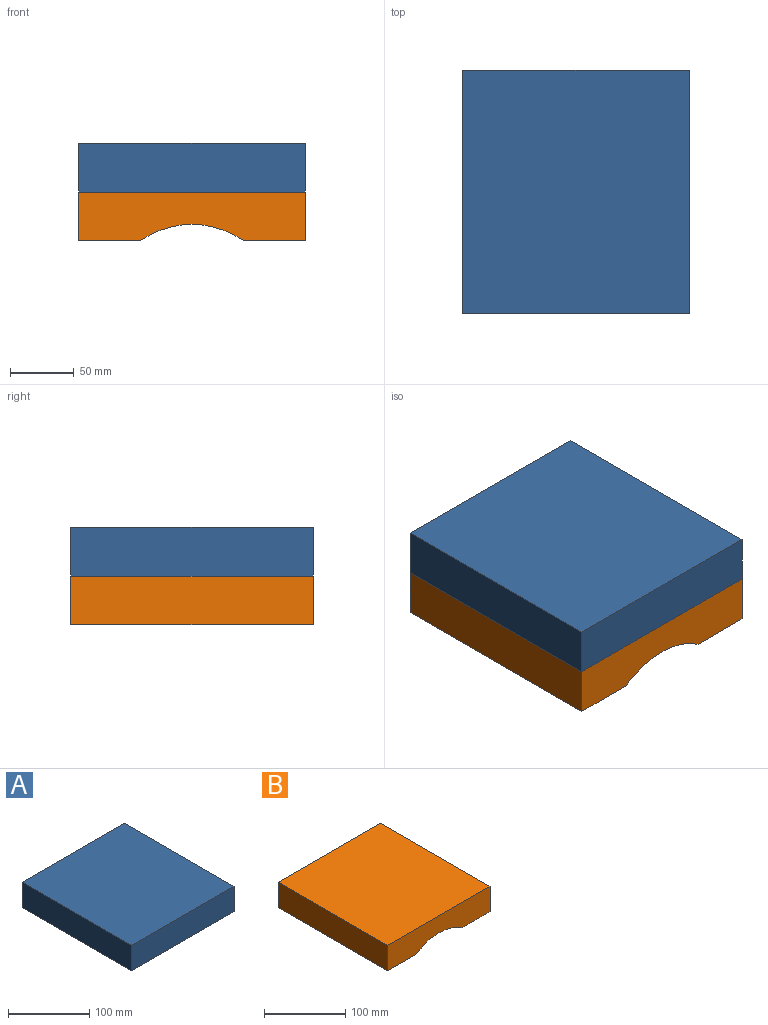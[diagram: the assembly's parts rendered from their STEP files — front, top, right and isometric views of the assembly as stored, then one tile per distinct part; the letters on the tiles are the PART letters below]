
ASSEMBLY  parts=2 mates=1
PART A: 6 faces, bbox 177.8x190.5x38.1 mm
  f0: plane 190.5x177.8mm, normal (0,0,-1), area 33870.9mm2, adj f1,f3,f4,f5
  f1: plane 190.5x38.1mm, normal (1,0,0), area 7258mm2, adj f0,f2,f4,f5
  f2: plane 190.5x177.8mm, normal (0,0,1), area 33870.9mm2, adj f1,f3,f4,f5
  f3: plane 190.5x38.1mm, normal (-1,0,0), area 7258mm2, adj f0,f2,f4,f5
  f4: plane 177.8x38.1mm, normal (0,1,0), area 6774.2mm2, adj f0,f1,f2,f3
  f5: plane 177.8x38.1mm, normal (0,-1,0), area 6774.2mm2, adj f0,f1,f2,f3
PART B: 8 faces, bbox 177.8x190.5x38.1 mm
  f0: plane 190.5x38.1mm, normal (-1,0,0), area 7258mm2, adj f1,f5,f6,f7
  f1: plane 190.5x48.74mm, normal (0,0,-1), area 9284.8mm2, adj f0,f2,f6,f7
  f2: cylinder r=69.85mm len=190.5mm, axis (0,-1,0), area 16301.8mm2, adj f1,f3,f6,f7
  f3: plane 190.5x48.74mm, normal (0,0,-1), area 9284.8mm2, adj f2,f4,f6,f7
  f4: plane 190.5x38.1mm, normal (1,0,0), area 7258mm2, adj f3,f5,f6,f7
  f5: plane 190.5x177.8mm, normal (0,0,1), area 33870.9mm2, adj f0,f4,f6,f7
  f6: plane 177.8x38.1mm, normal (0,1,0), area 6080.7mm2, adj f0,f1,f2,f3,f4,f5
  f7: plane 177.8x38.1mm, normal (0,-1,0), area 6080.7mm2, adj f0,f1,f2,f3,f4,f5
PLACE A t=(31.26,-75.65,12.87)mm
PLACE B t=(-57.64,-75.65,-44.28)mm
MATE fastened A.f0 <-> B.f5  axis (0,0,-1) through (31.26,19.6,-6.18)mm
